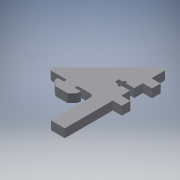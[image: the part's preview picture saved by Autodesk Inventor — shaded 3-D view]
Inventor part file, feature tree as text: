
AUTODESK INVENTOR PART (.ipt)
format: ipt  version: 2017 (Build 210142000, 142)  size: 389,632 bytes
history: native  units: mm
features: extrude x1, sketch x1
ambient origin geometry x8: Origin, YZ Plane, XZ Plane, XY Plane, X Axis, Y Axis, Z Axis, Center Point
bodies: Solid1 (feature_tree)
feature tree (2):
  extrude  "Extrusion1"  [1 undecoded]
  sketch  "Sketch1"  dims[d0=6.0mm d1=0.0mm]
note: 1 required parameter value undecoded (feature->parameter linkage not recoverable at this tier; creation-order binding heuristic only, values carry confidence <= 0.55)
